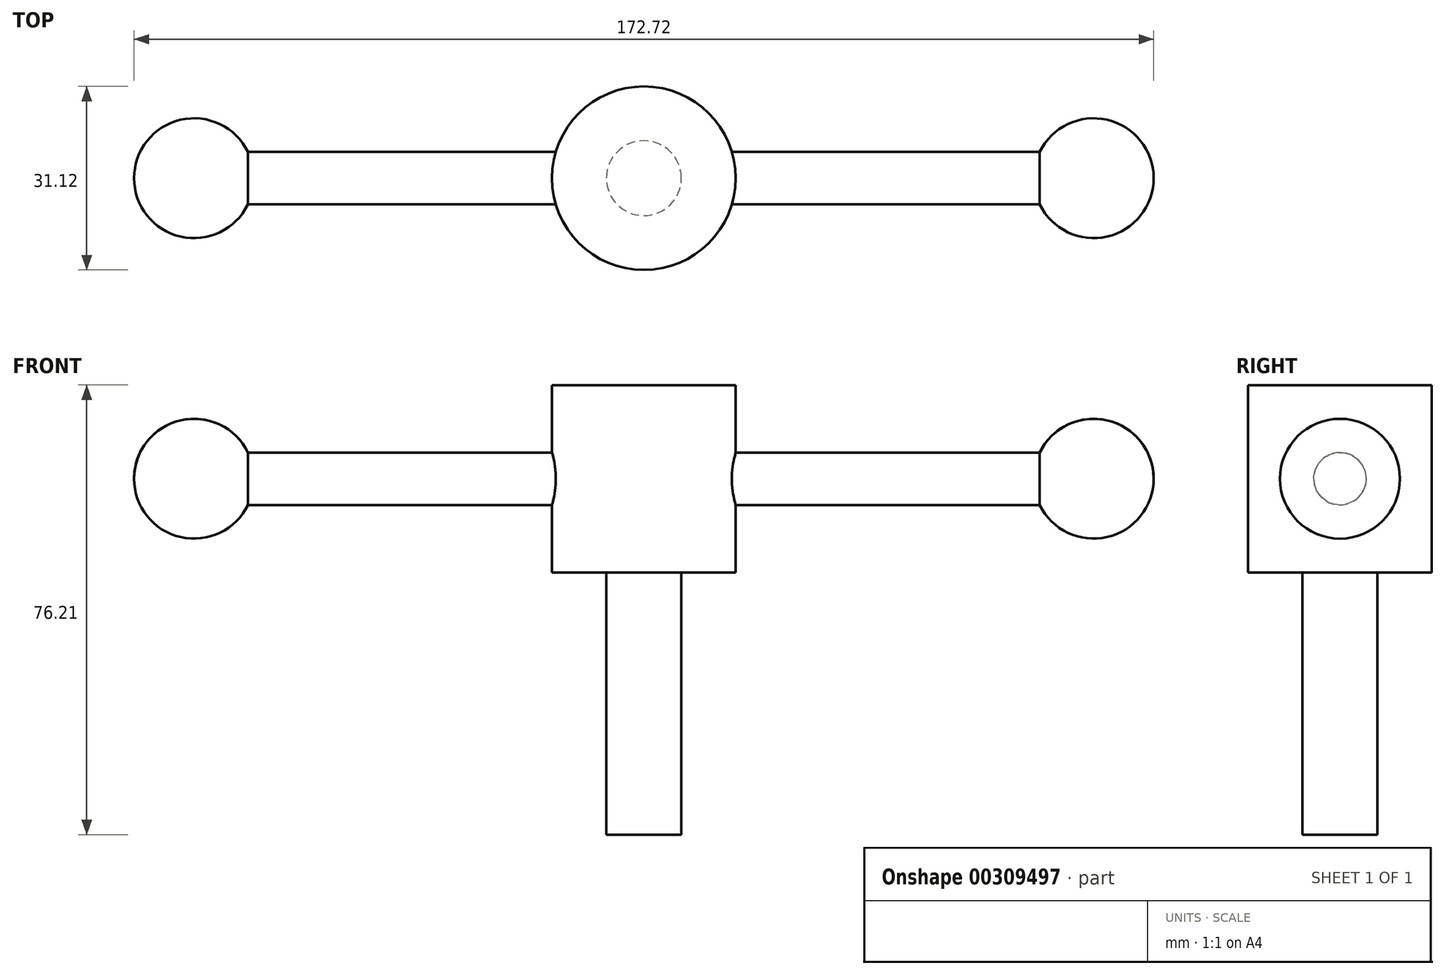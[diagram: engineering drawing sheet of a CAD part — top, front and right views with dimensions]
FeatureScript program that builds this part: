
annotation { "Feature Type Name" : "Feature", "Feature Type Description" : "" }
export const myFeature = defineFeature(function(context is Context, id is Id, definition is map)
    precondition{}
    {
        {
            var Q0;
            Q0=qCreatedBy(makeId("Front.planeOp"),FACE);
            var sketch = newSketch(context, id + "F0", { "sketchPlane" : qUnion([Q0])});
            skLineSegment(sketch, "E0", {"start": v(-66.04, 0) * mm, "end": v(66.04, 0) * mm});
            skArc(sketch, "E1", {"start": v(86.36, 0) * mm, "mid": v(76.2, 10.16) * mm, "end": v(66.04, 0) * mm});
            skArc(sketch, "E2", {"start": v(-66.04, 0) * mm, "mid": v(-76.2, 10.16) * mm, "end": v(-86.36, 0) * mm});
            skLineSegment(sketch, "E3", {"start": v(86.36, 0) * mm, "end": v(-86.36, 0) * mm});
            skLineSegment(sketch, "E4", {"start": v(-67.06, 4.44) * mm, "end": v(67.06, 4.44) * mm});
            skSolve(sketch);
        }
        {
            var Q0;
            Q0 = qSketchRegion(id + "F0", true);
            var Q1;
            Q1=sQuery(id+"F0.wireOp",EDGE,"E3");
            revolve(context, id + "F1", {"entities" : qUnion([Q0]), "axis" : qUnion([Q1]), "revolveType" : RevolveType.FULL});
        }
        {
            var Q0;
            Q0=qCreatedBy(makeId("Front.planeOp"),FACE);
            var sketch = newSketch(context, id + "F2", { "sketchPlane" : qUnion([Q0])});
            skLineSegment(sketch, "E5", {"start": v(0, 15.88) * mm, "end": v(-15.56, 15.87) * mm});
            skLineSegment(sketch, "E6", {"start": v(-15.56, 15.87) * mm, "end": v(-15.56, -15.87) * mm});
            skLineSegment(sketch, "E7", {"start": v(-15.56, -15.88) * mm, "end": v(0, -15.88) * mm});
            skLineSegment(sketch, "E8", {"start": v(0, -15.88) * mm, "end": v(0, 15.88) * mm});
            skLineSegment(sketch, "E9", {"start": v(0, -15.88) * mm, "end": v(0, -60.33) * mm});
            skLineSegment(sketch, "E10", {"start": v(0, -60.33) * mm, "end": v(-6.35, -60.33) * mm});
            skLineSegment(sketch, "E11", {"start": v(-6.35, -60.33) * mm, "end": v(-6.35, -15.88) * mm});
            skSolve(sketch);
        }
        {
            var Q0;
            Q0=makeQuery(id+"F2.imprint","IMPRINT",FACE,{"disambiguationData":[TD([[makeQuery(id+"F2.imprint","IMPRINT",EDGE,{"derivedFrom":sQuery(id+"F2.wireOp",EDGE,"E5")}),1.0]])]});
            var Q1;
            {var subQ0=sQuery(id+"F2.wireOp",EDGE,"E9");Q1=makeQuery(id+"F2.imprint","IMPRINT",FACE,{"disambiguationData":[TD([[makeQuery(id+"F2.imprint","IMPRINT",EDGE,{"derivedFrom":subQ0}),-1.0]])]});}
            var Q2;
            Q2=sQuery(id+"F2.wireOp",EDGE,"E9");
            revolve(context, id + "F3", {"operationType" : NewBodyOperationType.ADD, "entities" : qUnion([Q0, Q1]), "axis" : qUnion([Q2]), "revolveType" : RevolveType.FULL});
        }
    });
